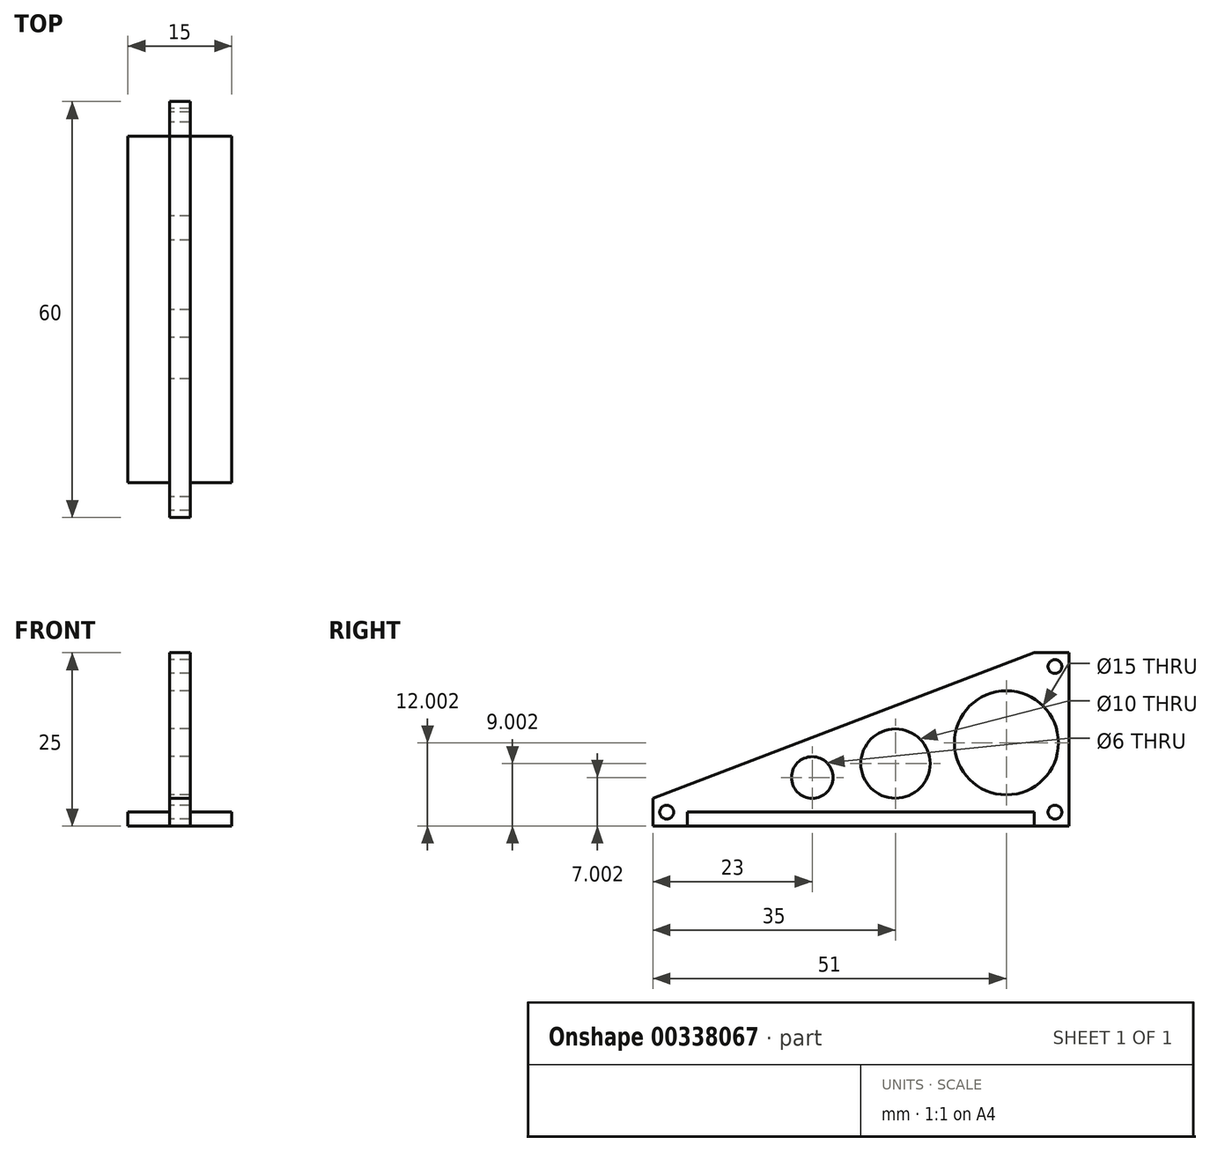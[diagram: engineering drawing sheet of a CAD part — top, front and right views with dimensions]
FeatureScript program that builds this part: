
annotation { "Feature Type Name" : "Feature", "Feature Type Description" : "" }
export const myFeature = defineFeature(function(context is Context, id is Id, definition is map)
    precondition{}
    {
        {
            var Q0;
            Q0=qCreatedBy(makeId("Right.planeOp"),FACE);
            var sketch = newSketch(context, id + "F0", { "sketchPlane" : qUnion([Q0])});
            skLineSegment(sketch, "E0", {"start": v(25, 14.04) * mm, "end": v(25, -10.96) * mm});
            skLineSegment(sketch, "E1", {"start": v(25, -10.96) * mm, "end": v(-35, -10.96) * mm});
            skLineSegment(sketch, "E2", {"start": v(25, 14.04) * mm, "end": v(20, 14.04) * mm});
            skLineSegment(sketch, "E3", {"start": v(-35, -10.96) * mm, "end": v(-35, -6.96) * mm});
            skLineSegment(sketch, "E4", {"start": v(-35, -6.96) * mm, "end": v(20, 14.04) * mm});
            skCircle(sketch, "E5", {"center": v(-12, -3.96) * mm, "radius": 3 * mm});
            skCircle(sketch, "E6", {"center": v(0, -1.96) * mm, "radius": 5 * mm});
            skCircle(sketch, "E7", {"center": v(16, 1.04) * mm, "radius": 7.5 * mm});
            skLineSegment(sketch, "E8", {"start": v(-30, -10.96) * mm, "end": v(-30, -8.96) * mm});
            skLineSegment(sketch, "E9", {"start": v(-30, -8.96) * mm, "end": v(20, -8.96) * mm});
            skLineSegment(sketch, "E10", {"start": v(20, -8.96) * mm, "end": v(20, -10.96) * mm});
            skCircle(sketch, "E11", {"center": v(23, 12.04) * mm, "radius": 1 * mm});
            skCircle(sketch, "E12", {"center": v(23, -8.96) * mm, "radius": 1 * mm});
            skCircle(sketch, "E13", {"center": v(-33, -8.96) * mm, "radius": 1 * mm});
            skPoint(sketch, "E14", {"position": v(-35, -8.96) * mm});
            skSolve(sketch);
        }
        {
            var Q0;
            {var subQ0=sQuery(id+"F0.wireOp",EDGE,"E8");Q0=makeQuery(id+"F0.imprint","IMPRINT",FACE,{"disambiguationData":[TD([[makeQuery(id+"F0.imprint","IMPRINT",EDGE,{"derivedFrom":subQ0}),-1.0]])]});}
            extrude(context, id + "F1", {"entities" : qUnion([Q0]), "endBound" : BoundingType.SYMMETRIC, "depth" : 15 * mm});
        }
        {
            var Q0;
            {var subQ2=sQuery(id+"F0.wireOp",EDGE,"E0");Q0=makeQuery(id+"F0.imprint","IMPRINT",FACE,{"disambiguationData":[TD([[makeQuery(id+"F0.imprint","IMPRINT",EDGE,{"derivedFrom":subQ2}),-1.0]])]});}
            extrude(context, id + "F2", {"entities" : qUnion([Q0]), "operationType" : NewBodyOperationType.ADD, "endBound" : BoundingType.SYMMETRIC, "depth" : 3 * mm});
        }
    });
